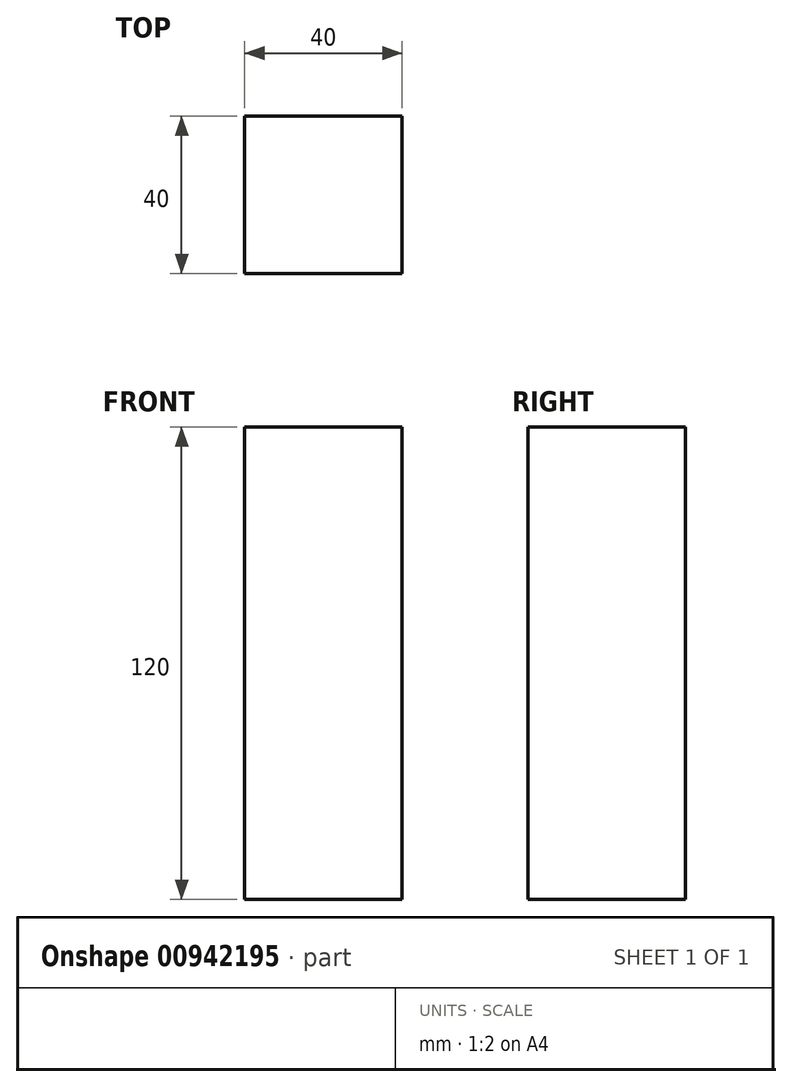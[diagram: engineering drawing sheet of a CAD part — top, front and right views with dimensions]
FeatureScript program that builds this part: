
annotation { "Feature Type Name" : "Feature", "Feature Type Description" : "" }
export const myFeature = defineFeature(function(context is Context, id is Id, definition is map)
    precondition{}
    {
        {
            assignVariable(context, id + "F0", {"name" : "profundidad", "anyValue" : 120});
        }
        {
            var Q0;
            Q0=qCreatedBy(makeId("Top.planeOp"),FACE);
            var sketch = newSketch(context, id + "F1", { "sketchPlane" : qUnion([Q0])});
            skLineSegment(sketch, "E0.bottom", {"start": v(-20, 20) * mm, "end": v(20, 20) * mm});
            skLineSegment(sketch, "E0.top", {"start": v(-20, -20) * mm, "end": v(20, -20) * mm});
            skLineSegment(sketch, "E0.left", {"start": v(-20, 20) * mm, "end": v(-20, -20) * mm});
            skLineSegment(sketch, "E0.right", {"start": v(20, 20) * mm, "end": v(20, -20) * mm});
            skSolve(sketch);
        }
        {
            var Q0;
            Q0=makeQuery(id+"F1.imprint","IMPRINT",FACE,{"disambiguationData":[TD([[makeQuery(id+"F1.imprint","IMPRINT",EDGE,{"derivedFrom":sQuery(id+"F1.wireOp",EDGE,"E0.bottom")}),-1.0]])]});
            extrude(context, id + "F2", {"entities" : qUnion([Q0]), "endBound" : BoundingType.SYMMETRIC, "depth" : (getVariable(context, 'profundidad')) * mm, "offsetDistance" : 25 * mm});
        }
    });
